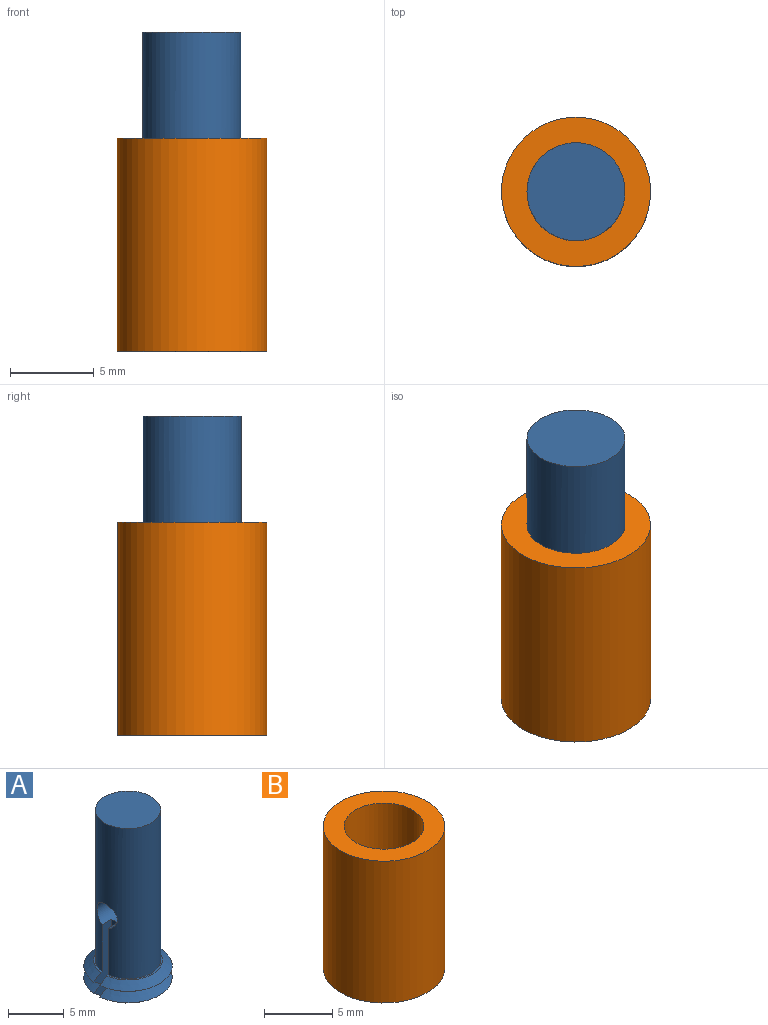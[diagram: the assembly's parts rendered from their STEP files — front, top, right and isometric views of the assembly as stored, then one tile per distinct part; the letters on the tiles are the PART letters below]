
ASSEMBLY  parts=2 mates=1
PART A: 23 faces, bbox 7.9x7.9x19.1 mm
  f0: cone r=3.97mm half-angle=54.2deg, axis (0,0,1), area 11.2mm2, adj f1,f13,f17,f20
  f1: cone r=3.09mm half-angle=54.2deg, axis (0,0,-1), area 11.2mm2, adj f0,f2,f17,f20
  f2: cone r=3.97mm half-angle=54.2deg, axis (0,0,1), area 11.2mm2, adj f1,f3,f17,f20
  f3: cone r=3.09mm half-angle=54.2deg, axis (0,0,-1), area 11.2mm2, adj f2,f4,f17,f20
  f4: plane 6.13x2.71mm, normal (0,0,1), area 1.4mm2, adj f3,f6,f17,f20
  f5: cylinder r=1.27mm len=2.54mm, axis (-1,0,0), area 18.1mm2, adj f6,f19,f20,f21,f22
  f6: cylinder r=2.92mm len=16.51mm, axis (0,0,-1), area 288.2mm2, adj f4,f5,f11,f12,f14,f16,f17,f20
  f7: cone r=3.97mm half-angle=54.2deg, axis (0,0,1), area 11.2mm2, adj f8,f13,f16,f21
  f8: cone r=3.09mm half-angle=54.2deg, axis (0,0,-1), area 11.2mm2, adj f7,f9,f16,f21
  f9: cone r=3.97mm half-angle=54.2deg, axis (0,0,1), area 11.2mm2, adj f8,f10,f16,f21
  f10: cone r=3.09mm half-angle=54.2deg, axis (0,0,-1), area 11.2mm2, adj f9,f11,f16,f21
  f11: plane 6.13x2.71mm, normal (0,0,1), area 1.4mm2, adj f6,f10,f16,f21
  f12: plane 5.84x5.84mm, normal (0,0,1), area 26.8mm2, adj f6
  f13: plane 6.17x6.13mm, normal (0,0,-1), area 27.8mm2, adj f0,f7,f16,f17,f18,f20,f21,f22
  f14: cylinder r=1.27mm len=2.54mm, axis (1,0,0), area 18.1mm2, adj f6,f15,f16,f17,f18
  f15: plane 2.54x2.54mm, normal (1,0,0), area 5.1mm2, adj f14
  f16: plane 3.25x2.31mm, normal (0,1,0), area 5.6mm2, adj f6,f7,f8,f9,f10,f11,f13,f14
  f17: plane 3.25x2.31mm, normal (0,-1,0), area 5.6mm2, adj f0,f1,f2,f3,f4,f6,f13,f14
  f18: plane 3.23x0.76mm, normal (1,0,0), area 2.4mm2, adj f13,f14,f16,f17
  f19: plane 2.54x2.54mm, normal (-1,0,0), area 5.1mm2, adj f5
  f20: plane 7.69x2.31mm, normal (0,-1,0), area 11.1mm2, adj f0,f1,f2,f3,f4,f5,f6,f13
  f21: plane 7.69x2.31mm, normal (0,1,0), area 11.1mm2, adj f5,f6,f7,f8,f9,f10,f11,f13
  f22: plane 7.68x0.76mm, normal (-1,0,0), area 5.8mm2, adj f5,f13,f20,f21
PART B: 9 faces, bbox 8.9x8.9x12.7 mm
  f0: cone r=3.09mm half-angle=54.2deg, axis (0,0,-1), area 24.1mm2, adj f1,f8
  f1: cone r=3.97mm half-angle=54.2deg, axis (0,0,1), area 24.1mm2, adj f0,f2
  f2: plane 8.89x8.89mm, normal (0,0,-1), area 32.1mm2, adj f1,f3
  f3: cylinder r=4.45mm len=12.7mm, axis (0,0,-1), area 354.7mm2, adj f2,f4
  f4: plane 8.89x8.89mm, normal (0,0,1), area 35.3mm2, adj f3,f5
  f5: cylinder r=2.92mm len=10.16mm, axis (0,0,-1), area 186.5mm2, adj f4,f6
  f6: plane 6.17x6.17mm, normal (0,0,-1), area 3.1mm2, adj f5,f7
  f7: cone r=3.09mm half-angle=54.2deg, axis (0,0,-1), area 24.1mm2, adj f6,f8
  f8: cone r=3.97mm half-angle=54.2deg, axis (0,0,1), area 24.1mm2, adj f0,f7
PLACE A at identity fixed
PLACE B rot(axis=(0,0,-1),90deg) t=(0,0,0.03)mm
MATE slider B.f0 <-> A.f0  axis (0,0,-1) through (0,0,6.38)mm
